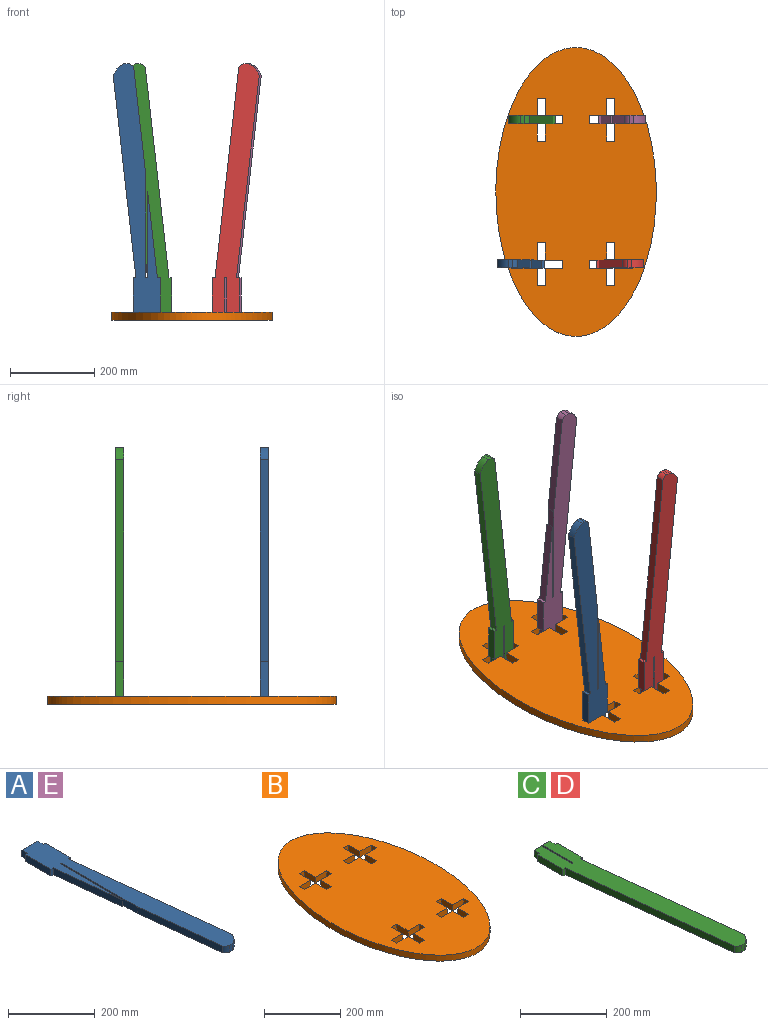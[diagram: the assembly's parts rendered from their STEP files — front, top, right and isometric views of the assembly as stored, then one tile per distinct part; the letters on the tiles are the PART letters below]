
ASSEMBLY  parts=5 mates=1
PART A: 20 faces, bbox 111.6x609.6x19.1 mm
  f0: extruded ~19.05x11.94mm, area 294mm2, adj f1,f17,f18,f19
  f1: plane 19.05x9.39mm, normal (0,-1,0), area 178.9mm2, adj f0,f2,f18,f19
  f2: extruded ~28.64x27.27mm, area 782.9mm2, adj f1,f3,f18,f19
  f3: plane 479.36x53.96mm, normal (0.99,0.11,0), area 9189.5mm2, adj f2,f4,f18,f19
  f4: plane 19.05x6.85mm, normal (0,-1,0), area 130.5mm2, adj f3,f5,f18,f19
  f5: plane 82.55x19.05mm, normal (1,0,0), area 1572.6mm2, adj f4,f6,f18,f19
  f6: plane 19.05x6.85mm, normal (0,1,0), area 130.5mm2, adj f5,f7,f18,f19
  f7: plane 19.05x19.05mm, normal (1,0,0), area 362.9mm2, adj f6,f8,f18,f19
  f8: plane 50.89x19.05mm, normal (0,1,0), area 969.4mm2, adj f7,f9,f18,f19
  f9: plane 19.05x19.05mm, normal (-1,0,0), area 362.9mm2, adj f8,f10,f18,f19
  f10: plane 19.05x6.78mm, normal (0,1,0), area 129.1mm2, adj f9,f11,f18,f19
  f11: plane 82.55x19.05mm, normal (-1,0,0), area 1572.6mm2, adj f10,f12,f18,f19
  f12: plane 19.05x6.78mm, normal (0,-1,0), area 129.1mm2, adj f11,f13,f18,f19
  f13: plane 204.55x23.06mm, normal (-0.99,-0.11,0), area 3921.4mm2, adj f12,f14,f18,f19
  f14: plane 204.55x19.05mm, normal (1,0,0), area 3896.7mm2, adj f13,f15,f18,f19
  f15: plane 19.05x4.76mm, normal (0,-1,0), area 90.7mm2, adj f14,f16,f18,f19
  f16: plane 246.8x19.05mm, normal (-1,0,0), area 4701.5mm2, adj f15,f17,f18,f19
  f17: plane 252.04x28.42mm, normal (-0.99,-0.11,0), area 4831.9mm2, adj f0,f16,f18,f19
  f18: plane 609.6x111.62mm, normal (0,0,1), area 30702.9mm2, adj f0,f1,f2,f3,f4,f5,f6,f7
  f19: plane 609.6x111.62mm, normal (0,0,-1), area 30702.9mm2, adj f0,f1,f2,f3,f4,f5,f6,f7
PART B: 51 faces, bbox 381x685.8x19.1 mm
  f0: plane 685.8x381mm, normal (0,0,1), area 191184.3mm2, adj f2,f3,f4,f5,f6,f7,f8,f9
  f1: plane 685.8x381mm, normal (0,0,-1), area 191184.3mm2, adj f2,f3,f4,f5,f6,f7,f8,f9
  f2: extruded ~685.8x381mm, area 32577.9mm2, adj f0,f1
  f3: plane 19.05x19.05mm, normal (1,0,0), area 362.9mm2, adj f0,f1,f4,f14
  f4: plane 41.28x19.05mm, normal (0,1,0), area 786.3mm2, adj f0,f1,f3,f5
  f5: plane 41.28x19.05mm, normal (1,0,0), area 786.3mm2, adj f0,f1,f4,f6
  f6: plane 19.05x19.05mm, normal (0,1,0), area 362.9mm2, adj f0,f1,f5,f7
  f7: plane 41.28x19.05mm, normal (-1,0,0), area 786.3mm2, adj f0,f1,f6,f8
  f8: plane 41.28x19.05mm, normal (0,1,0), area 786.3mm2, adj f0,f1,f7,f9
  f9: plane 19.05x19.05mm, normal (-1,0,0), area 362.9mm2, adj f0,f1,f8,f10
  f10: plane 41.28x19.05mm, normal (0,-1,0), area 786.3mm2, adj f0,f1,f9,f11
  f11: plane 41.28x19.05mm, normal (-1,0,0), area 786.3mm2, adj f0,f1,f10,f12
  f12: plane 19.05x19.05mm, normal (0,-1,0), area 362.9mm2, adj f0,f1,f11,f13
  f13: plane 41.28x19.05mm, normal (1,0,0), area 786.3mm2, adj f0,f1,f12,f14
  f14: plane 41.28x19.05mm, normal (0,-1,0), area 786.3mm2, adj f0,f1,f3,f13
  f15: plane 19.05x19.05mm, normal (-1,0,0), area 362.9mm2, adj f0,f1,f16,f26
  f16: plane 41.28x19.05mm, normal (0,-1,0), area 786.3mm2, adj f0,f1,f15,f17
  f17: plane 41.28x19.05mm, normal (-1,0,0), area 786.3mm2, adj f0,f1,f16,f18
  f18: plane 19.05x19.05mm, normal (0,-1,0), area 362.9mm2, adj f0,f1,f17,f19
  f19: plane 41.28x19.05mm, normal (1,0,0), area 786.3mm2, adj f0,f1,f18,f20
  f20: plane 41.28x19.05mm, normal (0,-1,0), area 786.3mm2, adj f0,f1,f19,f21
  f21: plane 19.05x19.05mm, normal (1,0,0), area 362.9mm2, adj f0,f1,f20,f22
  f22: plane 41.28x19.05mm, normal (0,1,0), area 786.3mm2, adj f0,f1,f21,f23
  f23: plane 41.28x19.05mm, normal (1,0,0), area 786.3mm2, adj f0,f1,f22,f24
  f24: plane 19.05x19.05mm, normal (0,1,0), area 362.9mm2, adj f0,f1,f23,f25
  f25: plane 41.28x19.05mm, normal (-1,0,0), area 786.3mm2, adj f0,f1,f24,f26
  f26: plane 41.28x19.05mm, normal (0,1,0), area 786.3mm2, adj f0,f1,f15,f25
  f27: plane 19.05x19.05mm, normal (-1,0,0), area 362.9mm2, adj f0,f1,f28,f38
  f28: plane 41.28x19.05mm, normal (0,-1,0), area 786.3mm2, adj f0,f1,f27,f29
  f29: plane 41.28x19.05mm, normal (-1,0,0), area 786.3mm2, adj f0,f1,f28,f30
  f30: plane 19.05x19.05mm, normal (0,-1,0), area 362.9mm2, adj f0,f1,f29,f31
  f31: plane 41.28x19.05mm, normal (1,0,0), area 786.3mm2, adj f0,f1,f30,f32
  f32: plane 41.28x19.05mm, normal (0,-1,0), area 786.3mm2, adj f0,f1,f31,f33
  f33: plane 19.05x19.05mm, normal (1,0,0), area 362.9mm2, adj f0,f1,f32,f34
  f34: plane 41.28x19.05mm, normal (0,1,0), area 786.3mm2, adj f0,f1,f33,f35
  f35: plane 41.28x19.05mm, normal (1,0,0), area 786.3mm2, adj f0,f1,f34,f36
  f36: plane 19.05x19.05mm, normal (0,1,0), area 362.9mm2, adj f0,f1,f35,f37
  f37: plane 41.28x19.05mm, normal (-1,0,0), area 786.3mm2, adj f0,f1,f36,f38
  f38: plane 41.28x19.05mm, normal (0,1,0), area 786.3mm2, adj f0,f1,f27,f37
  f39: plane 41.28x19.05mm, normal (0,1,0), area 786.3mm2, adj f0,f1,f40,f50
  f40: plane 19.05x19.05mm, normal (-1,0,0), area 362.9mm2, adj f0,f1,f39,f41
  f41: plane 41.28x19.05mm, normal (0,-1,0), area 786.3mm2, adj f0,f1,f40,f42
  f42: plane 41.28x19.05mm, normal (-1,0,0), area 786.3mm2, adj f0,f1,f41,f43
  f43: plane 19.05x19.05mm, normal (0,-1,0), area 362.9mm2, adj f0,f1,f42,f44
  f44: plane 41.28x19.05mm, normal (1,0,0), area 786.3mm2, adj f0,f1,f43,f45
  f45: plane 41.28x19.05mm, normal (0,-1,0), area 786.3mm2, adj f0,f1,f44,f46
  f46: plane 19.05x19.05mm, normal (1,0,0), area 362.9mm2, adj f0,f1,f45,f47
  f47: plane 41.28x19.05mm, normal (0,1,0), area 786.3mm2, adj f0,f1,f46,f48
  f48: plane 41.28x19.05mm, normal (1,0,0), area 786.3mm2, adj f0,f1,f47,f49
  f49: plane 19.05x19.05mm, normal (0,1,0), area 362.9mm2, adj f0,f1,f48,f50
  f50: plane 41.28x19.05mm, normal (-1,0,0), area 786.3mm2, adj f0,f1,f39,f49
PART C: 20 faces, bbox 111.6x609.6x19.1 mm
  f0: plane 498.84x56.24mm, normal (-0.99,-0.11,0), area 9563.1mm2, adj f1,f17,f18,f19
  f1: extruded ~19.05x11.94mm, area 294mm2, adj f0,f2,f18,f19
  f2: plane 19.05x9.39mm, normal (0,-1,0), area 178.9mm2, adj f1,f3,f18,f19
  f3: extruded ~28.64x27.27mm, area 782.9mm2, adj f2,f4,f18,f19
  f4: plane 479.36x53.96mm, normal (0.99,0.11,0), area 9189.5mm2, adj f3,f5,f18,f19
  f5: plane 19.05x6.85mm, normal (0,-1,0), area 130.5mm2, adj f4,f6,f18,f19
  f6: plane 82.55x19.05mm, normal (1,0,0), area 1572.6mm2, adj f5,f7,f18,f19
  f7: plane 19.05x6.85mm, normal (0,1,0), area 130.5mm2, adj f6,f8,f18,f19
  f8: plane 19.05x19.05mm, normal (1,0,0), area 362.9mm2, adj f7,f9,f18,f19
  f9: plane 23.06x19.05mm, normal (0,1,0), area 439.3mm2, adj f8,f10,f18,f19
  f10: plane 101.6x19.05mm, normal (-1,0,0), area 1935.5mm2, adj f9,f11,f18,f19
  f11: plane 19.05x4.76mm, normal (0,1,0), area 90.7mm2, adj f10,f12,f18,f19
  f12: plane 101.6x19.05mm, normal (1,0,0), area 1935.5mm2, adj f11,f13,f18,f19
  f13: plane 23.06x19.05mm, normal (0,1,0), area 439.3mm2, adj f12,f14,f18,f19
  f14: plane 19.05x19.05mm, normal (-1,0,0), area 362.9mm2, adj f13,f15,f18,f19
  f15: plane 19.05x6.78mm, normal (0,1,0), area 129.1mm2, adj f14,f16,f18,f19
  f16: plane 82.55x19.05mm, normal (-1,0,0), area 1572.6mm2, adj f15,f17,f18,f19
  f17: plane 19.05x6.78mm, normal (0,-1,0), area 129.1mm2, adj f0,f16,f18,f19
  f18: plane 609.6x111.62mm, normal (0,0,1), area 31293.8mm2, adj f0,f1,f2,f3,f4,f5,f6,f7
  f19: plane 609.6x111.62mm, normal (0,0,-1), area 31293.8mm2, adj f0,f1,f2,f3,f4,f5,f6,f7
PART D: same geometry as C
PART E: same geometry as A
PLACE A rot(axis=(0,0.71,-0.71),180deg) t=(-193.41,-96.43,137.89)mm
PLACE B rot(axis=(-0.12,0.01,0.99),0deg) t=(-135.82,65.49,82.06)mm
PLACE C rot(axis=(0,0.71,-0.71),180deg) t=(-170.55,246.38,137.89)mm
PLACE D rot(axis=(-1,0,0),90deg) t=(-101.14,-115.4,137.89)mm
PLACE E rot(axis=(-1,0,0),90deg) t=(-101.14,227.39,137.89)mm
MATE fastened A.f7 <-> B.f33  axis (-1,0,0) through (-269.04,-105.96,91.59)mm
